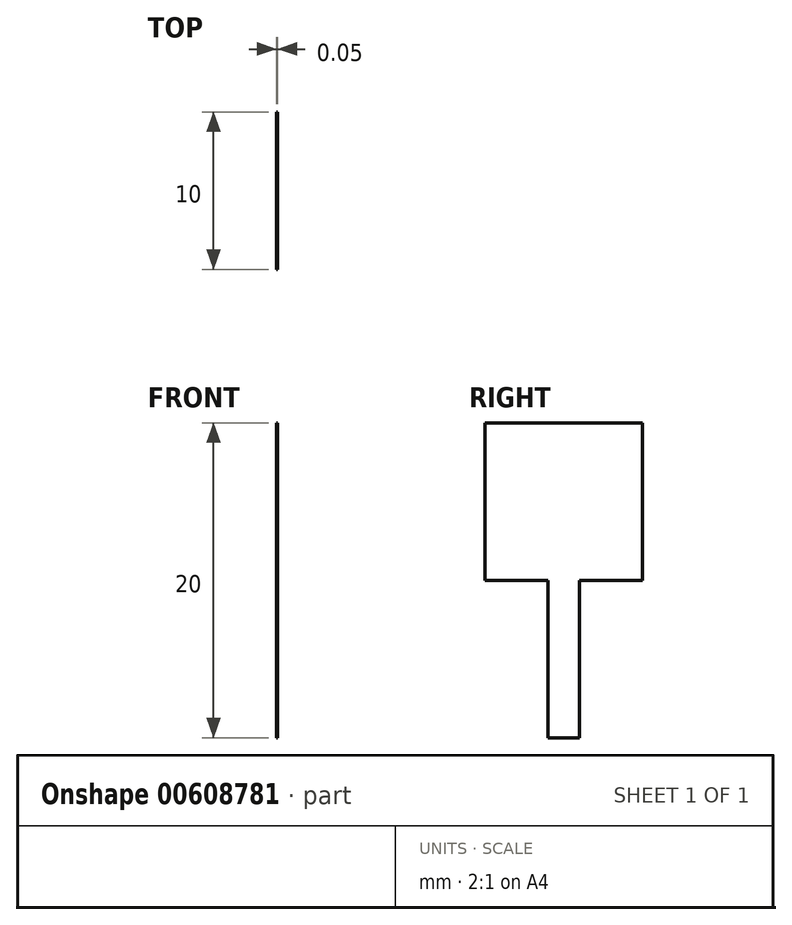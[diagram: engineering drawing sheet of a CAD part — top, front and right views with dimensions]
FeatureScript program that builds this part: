
annotation { "Feature Type Name" : "Feature", "Feature Type Description" : "" }
export const myFeature = defineFeature(function(context is Context, id is Id, definition is map)
    precondition{}
    {
        {
            var Q0;
            Q0=qCreatedBy(makeId("Right.planeOp"),FACE);
            var sketch = newSketch(context, id + "F0", { "sketchPlane" : qUnion([Q0])});
            skLineSegment(sketch, "E0.bottom", {"start": v(0, 0) * mm, "end": v(10, 0) * mm});
            skLineSegment(sketch, "E0.top", {"start": v(0, -10) * mm, "end": v(4, -10) * mm});
            skLineSegment(sketch, "E0.left", {"start": v(0, 0) * mm, "end": v(0, -10) * mm});
            skLineSegment(sketch, "E0.right", {"start": v(10, 0) * mm, "end": v(10, -10) * mm});
            skLineSegment(sketch, "E1.0", {"start": v(4, -10) * mm, "end": v(4, -20) * mm});
            skLineSegment(sketch, "E2.0", {"start": v(6, -10) * mm, "end": v(6, -20) * mm});
            skLineSegment(sketch, "E3", {"start": v(4, -20) * mm, "end": v(6, -20) * mm});
            skLineSegment(sketch, "E4.trimOffspring", {"start": v(6, -10) * mm, "end": v(10, -10) * mm});
            skSolve(sketch);
        }
        {
            var Q0;
            Q0=makeQuery(id+"F0.imprint","IMPRINT",FACE,{"disambiguationData":[TD([[makeQuery(id+"F0.imprint","IMPRINT",EDGE,{"derivedFrom":sQuery(id+"F0.wireOp",EDGE,"E0.bottom")}),-1.0]])]});
            extrude(context, id + "F1", {"entities" : qUnion([Q0]), "depth" : 0.05 * mm, "offsetDistance" : 25 * mm});
        }
    });
